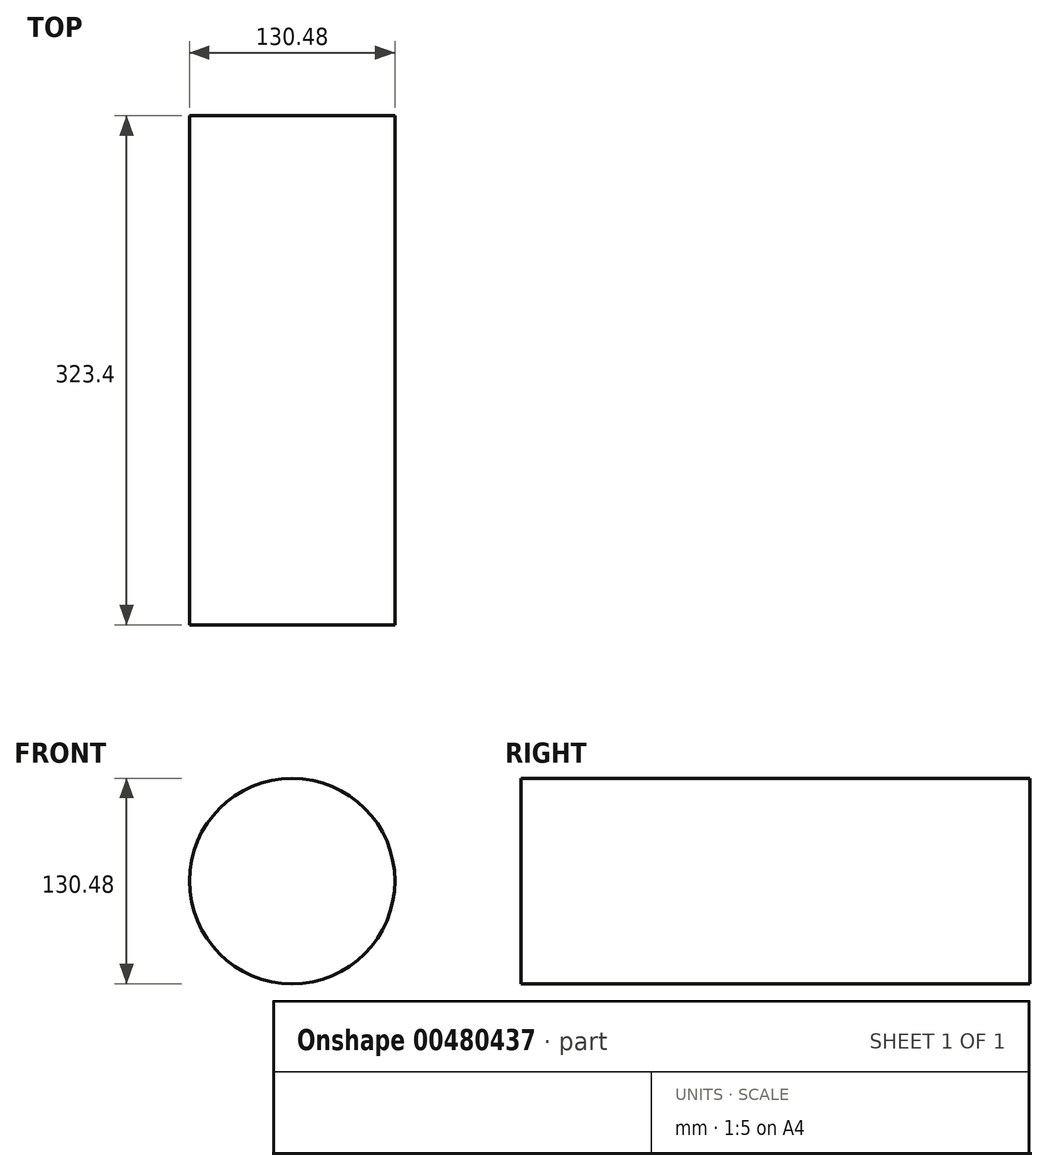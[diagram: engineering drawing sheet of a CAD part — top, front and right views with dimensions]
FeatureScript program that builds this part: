
annotation { "Feature Type Name" : "Feature", "Feature Type Description" : "" }
export const myFeature = defineFeature(function(context is Context, id is Id, definition is map)
    precondition{}
    {
        {
            var Q0;
            Q0=qCreatedBy(makeId("Right.planeOp"),FACE);
            var sketch = newSketch(context, id + "F0", { "sketchPlane" : qUnion([Q0])});
            skLineSegment(sketch, "E0.bottom", {"start": v(-72.3, 80.18) * mm, "end": v(251.1, 80.18) * mm});
            skLineSegment(sketch, "E0.top", {"start": v(-72.3, 14.94) * mm, "end": v(251.1, 14.94) * mm});
            skLineSegment(sketch, "E0.left", {"start": v(-72.3, 80.18) * mm, "end": v(-72.3, 14.94) * mm});
            skLineSegment(sketch, "E0.right", {"start": v(251.1, 80.18) * mm, "end": v(251.1, 14.94) * mm});
            skPoint(sketch, "E0.middle", {"position": v(89.4, 47.56) * mm});
            skSolve(sketch);
        }
        {
            var Q0;
            Q0 = qSketchRegion(id + "F0", true);
            var sketch = newSketch(context, id + "F1", { "sketchPlane" : qUnion([Q0])});
            skSolve(sketch);
        }
        {
            var Q0;
            Q0 = qSketchRegion(id + "FjcGLd2RDG5PpLu_0", true);
            var Q1;
            Q1=makeQuery(id+"F1.imprint","IMPRINT",FACE,{"disambiguationData":[TD([[makeQuery(id+"F1.imprint","IMPRINT",EDGE,{"derivedFrom":makeQuery(id+"F0.imprint","IMPRINT",EDGE,{"derivedFrom":sQuery(id+"F0.wireOp",EDGE,"E0.bottom")})}),-1.0]])]});
            var Q2;
            Q2=sQuery(id+"F0.wireOp",EDGE,"E0.top");
            revolve(context, id + "F2", {"entities" : qUnion([Q0, Q1]), "axis" : qUnion([Q2]), "revolveType" : RevolveType.FULL});
        }
    });
